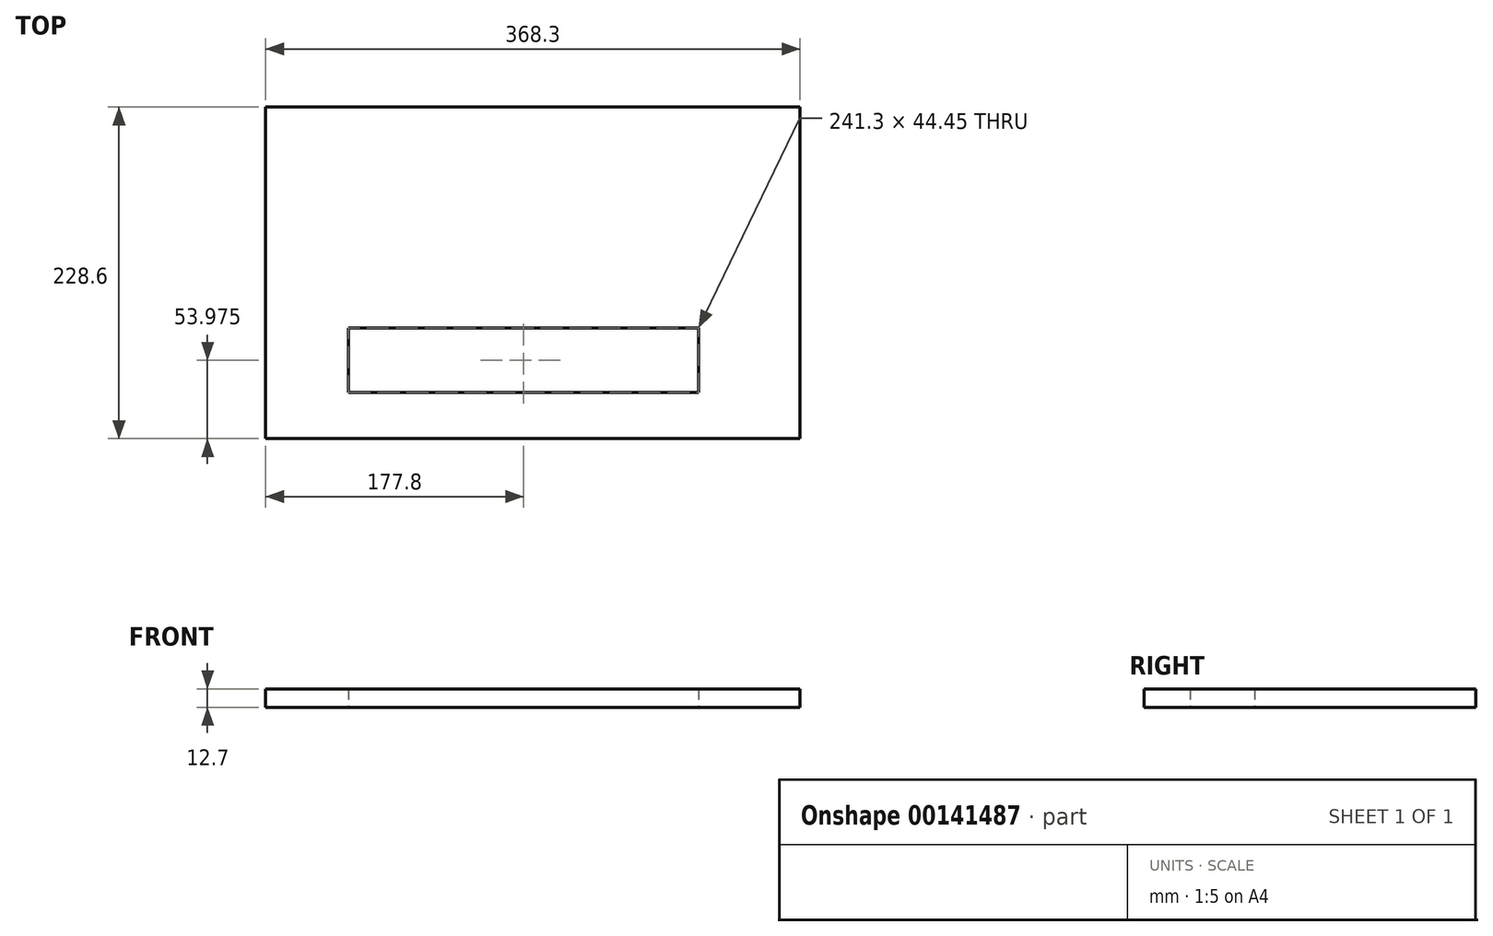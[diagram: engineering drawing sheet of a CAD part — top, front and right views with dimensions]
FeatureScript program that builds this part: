
annotation { "Feature Type Name" : "Feature", "Feature Type Description" : "" }
export const myFeature = defineFeature(function(context is Context, id is Id, definition is map)
    precondition{}
    {
        {
            var Q0;
            Q0=qCreatedBy(makeId("Top.planeOp"),FACE);
            var sketch = newSketch(context, id + "F0", { "sketchPlane" : qUnion([Q0])});
            skLineSegment(sketch, "E0.bottom", {"start": v(-184.15, 114.3) * mm, "end": v(184.15, 114.3) * mm});
            skLineSegment(sketch, "E0.top", {"start": v(-184.15, -114.3) * mm, "end": v(184.15, -114.3) * mm});
            skLineSegment(sketch, "E0.left", {"start": v(-184.15, 114.3) * mm, "end": v(-184.15, -114.3) * mm});
            skLineSegment(sketch, "E0.right", {"start": v(184.15, 114.3) * mm, "end": v(184.15, -114.3) * mm});
            skLineSegment(sketch, "E1.bottom", {"start": v(-127, -38.1) * mm, "end": v(114.3, -38.1) * mm});
            skLineSegment(sketch, "E1.top", {"start": v(-127, -82.55) * mm, "end": v(114.3, -82.55) * mm});
            skLineSegment(sketch, "E1.left", {"start": v(-127, -38.1) * mm, "end": v(-127, -82.55) * mm});
            skLineSegment(sketch, "E1.right", {"start": v(114.3, -38.1) * mm, "end": v(114.3, -82.55) * mm});
            skLineSegment(sketch, "E2", {"start": v(-184.15, -114.3) * mm, "end": v(184.15, 114.3) * mm, "construction": true});
            skSolve(sketch);
        }
        {
            var Q0;
            Q0=makeQuery(id+"F0.imprint","IMPRINT",FACE,{"disambiguationData":[TD([[makeQuery(id+"F0.imprint","IMPRINT",EDGE,{"derivedFrom":sQuery(id+"F0.wireOp",EDGE,"E0.bottom")}),-1.0]])]});
            extrude(context, id + "F1", {"entities" : qUnion([Q0]), "depth" : 12.7 * mm});
        }
    });
